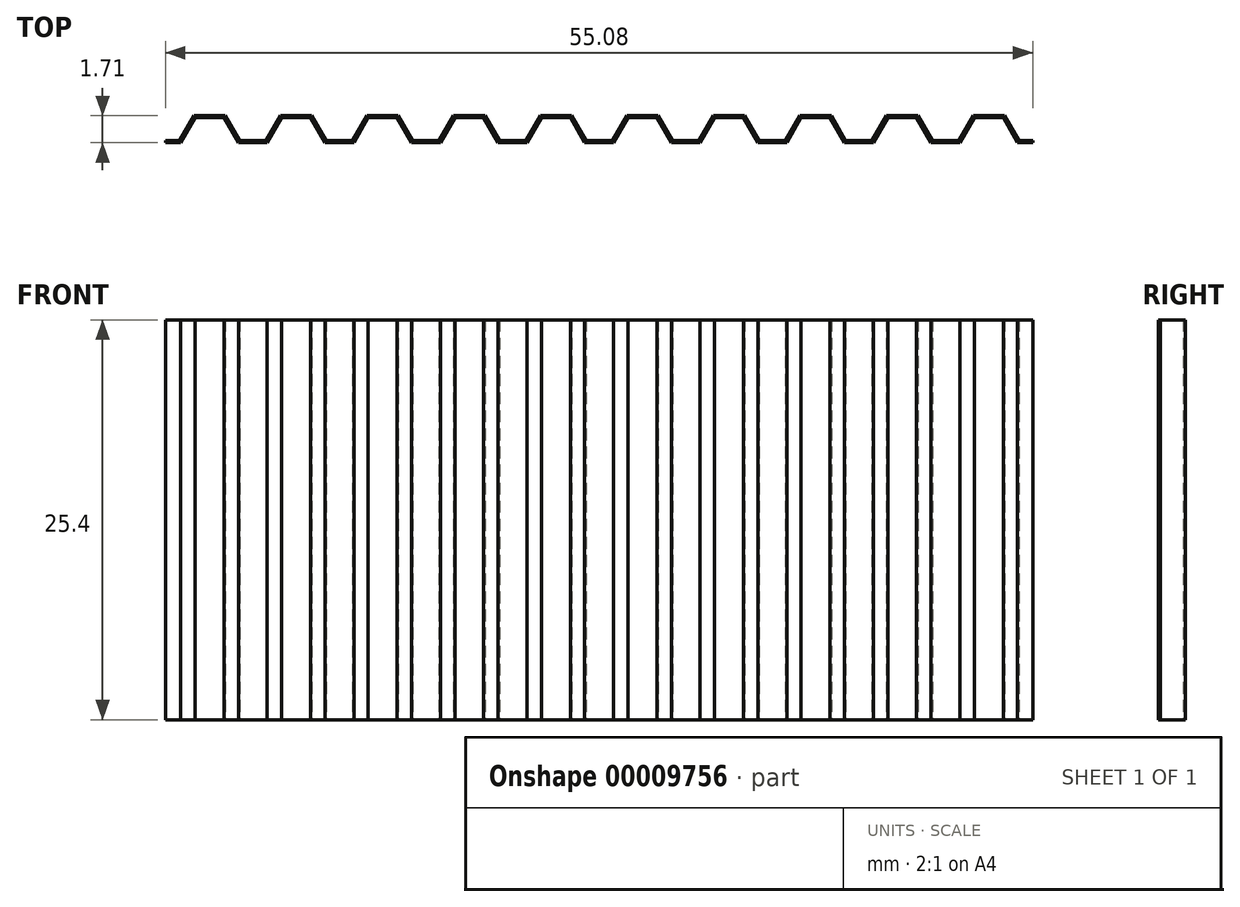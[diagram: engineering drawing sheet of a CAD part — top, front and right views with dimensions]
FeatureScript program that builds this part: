
annotation { "Feature Type Name" : "Feature", "Feature Type Description" : "" }
export const myFeature = defineFeature(function(context is Context, id is Id, definition is map)
    precondition{}
    {
        {
            var Q0;
            Q0=qCreatedBy(makeId("Top.planeOp"),FACE);
            var sketch = newSketch(context, id + "F0", { "sketchPlane" : qUnion([Q0])});
            skCircle(sketch, "E0.cCircle", {"center": v(0, 0) * mm, "radius": 1.59 * mm, "construction": true});
            skLineSegment(sketch, "E0.1", {"start": v(-1.83, 0) * mm, "end": v(-0.92, 1.59) * mm});
            skLineSegment(sketch, "E0.2", {"start": v(-0.92, 1.59) * mm, "end": v(0.92, 1.59) * mm});
            skLineSegment(sketch, "E0.3", {"start": v(0.92, 1.59) * mm, "end": v(1.83, 0) * mm});
            skLineSegment(sketch, "E1", {"start": v(1.83, 0) * mm, "end": v(3.67, 0) * mm});
            skLineSegment(sketch, "E2.1.0.0", {"start": v(6.42, 1.59) * mm, "end": v(7.33, 0) * mm});
            skLineSegment(sketch, "E2.1.0.1", {"start": v(7.33, 0) * mm, "end": v(9.17, 0) * mm});
            skLineSegment(sketch, "E2.1.0.2", {"start": v(3.67, 0) * mm, "end": v(4.58, 1.59) * mm});
            skLineSegment(sketch, "E2.1.0.3", {"start": v(4.58, 1.59) * mm, "end": v(6.42, 1.59) * mm});
            skLineSegment(sketch, "E2.direction1", {"start": v(1.83, 0) * mm, "end": v(7.33, 0) * mm, "construction": true});
            skLineSegment(sketch, "E3.1", {"start": v(7.4, 0.13) * mm, "end": v(9.1, 0.13) * mm});
            skLineSegment(sketch, "E3.2", {"start": v(6.49, 1.71) * mm, "end": v(7.4, 0.13) * mm});
            skLineSegment(sketch, "E3.3", {"start": v(4.5, 1.71) * mm, "end": v(6.49, 1.71) * mm});
            skLineSegment(sketch, "E3.4", {"start": v(3.6, 0.13) * mm, "end": v(4.5, 1.71) * mm});
            skLineSegment(sketch, "E3.5", {"start": v(1.9, 0.13) * mm, "end": v(3.6, 0.13) * mm});
            skLineSegment(sketch, "E3.6", {"start": v(0.99, 1.71) * mm, "end": v(1.9, 0.13) * mm});
            skLineSegment(sketch, "E3.7", {"start": v(-0.99, 1.71) * mm, "end": v(0.99, 1.71) * mm});
            skLineSegment(sketch, "E3.8", {"start": v(-1.9, 0.13) * mm, "end": v(-0.99, 1.71) * mm});
            skLineSegment(sketch, "E4", {"start": v(-1.83, 0) * mm, "end": v(-2.8, 0) * mm});
            skLineSegment(sketch, "E5.0.2.0", {"start": v(11.92, 1.59) * mm, "end": v(12.83, 0) * mm});
            skLineSegment(sketch, "E5.3.2.0", {"start": v(12.83, 0) * mm, "end": v(14.66, 0) * mm});
            skLineSegment(sketch, "E5.6.2.0", {"start": v(9.17, 0) * mm, "end": v(10.08, 1.59) * mm});
            skLineSegment(sketch, "E5.9.2.0", {"start": v(10.08, 1.59) * mm, "end": v(11.92, 1.59) * mm});
            skLineSegment(sketch, "E5.0.3.0", {"start": v(17.41, 1.59) * mm, "end": v(18.33, 0) * mm});
            skLineSegment(sketch, "E5.3.3.0", {"start": v(18.33, 0) * mm, "end": v(20.16, 0) * mm});
            skLineSegment(sketch, "E5.6.3.0", {"start": v(14.66, 0) * mm, "end": v(15.58, 1.59) * mm});
            skLineSegment(sketch, "E5.9.3.0", {"start": v(15.58, 1.59) * mm, "end": v(17.41, 1.59) * mm});
            skLineSegment(sketch, "E5.0.4.0", {"start": v(22.91, 1.59) * mm, "end": v(23.83, 0) * mm});
            skLineSegment(sketch, "E5.3.4.0", {"start": v(23.83, 0) * mm, "end": v(25.66, 0) * mm});
            skLineSegment(sketch, "E5.6.4.0", {"start": v(20.16, 0) * mm, "end": v(21.08, 1.59) * mm});
            skLineSegment(sketch, "E5.9.4.0", {"start": v(21.08, 1.59) * mm, "end": v(22.91, 1.59) * mm});
            skLineSegment(sketch, "E6.0", {"start": v(23.9, 0.13) * mm, "end": v(25.59, 0.13) * mm});
            skLineSegment(sketch, "E6.1", {"start": v(22.99, 1.71) * mm, "end": v(23.9, 0.13) * mm});
            skLineSegment(sketch, "E6.2", {"start": v(21, 1.71) * mm, "end": v(22.99, 1.71) * mm});
            skLineSegment(sketch, "E6.3", {"start": v(20.1, 0.13) * mm, "end": v(21, 1.71) * mm});
            skLineSegment(sketch, "E6.4", {"start": v(18.4, 0.13) * mm, "end": v(20.1, 0.13) * mm});
            skLineSegment(sketch, "E6.5", {"start": v(17.49, 1.71) * mm, "end": v(18.4, 0.13) * mm});
            skLineSegment(sketch, "E6.6", {"start": v(15.5, 1.71) * mm, "end": v(17.49, 1.71) * mm});
            skLineSegment(sketch, "E6.7", {"start": v(14.6, 0.13) * mm, "end": v(15.5, 1.71) * mm});
            skLineSegment(sketch, "E6.8", {"start": v(12.9, 0.13) * mm, "end": v(14.6, 0.13) * mm});
            skLineSegment(sketch, "E6.9", {"start": v(11.99, 1.71) * mm, "end": v(12.9, 0.13) * mm});
            skLineSegment(sketch, "E6.10", {"start": v(10, 1.71) * mm, "end": v(11.99, 1.71) * mm});
            skLineSegment(sketch, "E6.11", {"start": v(9.1, 0.13) * mm, "end": v(10, 1.71) * mm});
            skLineSegment(sketch, "E7.0.5.0", {"start": v(28.41, 1.59) * mm, "end": v(29.33, 0) * mm});
            skLineSegment(sketch, "E7.3.5.0", {"start": v(29.33, 0) * mm, "end": v(31.16, 0) * mm});
            skLineSegment(sketch, "E7.6.5.0", {"start": v(25.66, 0) * mm, "end": v(26.58, 1.59) * mm});
            skLineSegment(sketch, "E7.9.5.0", {"start": v(26.58, 1.59) * mm, "end": v(28.41, 1.59) * mm});
            skLineSegment(sketch, "E7.0.6.0", {"start": v(33.91, 1.59) * mm, "end": v(34.83, 0) * mm});
            skLineSegment(sketch, "E7.3.6.0", {"start": v(34.83, 0) * mm, "end": v(36.66, 0) * mm});
            skLineSegment(sketch, "E7.6.6.0", {"start": v(31.16, 0) * mm, "end": v(32.08, 1.59) * mm});
            skLineSegment(sketch, "E7.9.6.0", {"start": v(32.08, 1.59) * mm, "end": v(33.91, 1.59) * mm});
            skLineSegment(sketch, "E7.0.7.0", {"start": v(39.41, 1.59) * mm, "end": v(40.33, 0) * mm});
            skLineSegment(sketch, "E7.3.7.0", {"start": v(40.33, 0) * mm, "end": v(42.16, 0) * mm});
            skLineSegment(sketch, "E7.6.7.0", {"start": v(36.66, 0) * mm, "end": v(37.58, 1.59) * mm});
            skLineSegment(sketch, "E7.9.7.0", {"start": v(37.58, 1.59) * mm, "end": v(39.41, 1.59) * mm});
            skLineSegment(sketch, "E7.0.8.0", {"start": v(44.91, 1.59) * mm, "end": v(45.83, 0) * mm});
            skLineSegment(sketch, "E7.3.8.0", {"start": v(45.83, 0) * mm, "end": v(47.66, 0) * mm});
            skLineSegment(sketch, "E7.6.8.0", {"start": v(42.16, 0) * mm, "end": v(43.08, 1.59) * mm});
            skLineSegment(sketch, "E7.9.8.0", {"start": v(43.08, 1.59) * mm, "end": v(44.91, 1.59) * mm});
            skLineSegment(sketch, "E7.0.9.0", {"start": v(50.41, 1.59) * mm, "end": v(51.33, 0) * mm});
            skLineSegment(sketch, "E7.6.9.0", {"start": v(47.66, 0) * mm, "end": v(48.58, 1.59) * mm});
            skLineSegment(sketch, "E7.9.9.0", {"start": v(48.58, 1.59) * mm, "end": v(50.41, 1.59) * mm});
            skLineSegment(sketch, "E8.0", {"start": v(51.4, 0.13) * mm, "end": v(52.28, 0.13) * mm});
            skLineSegment(sketch, "E8.1", {"start": v(50.48, 1.71) * mm, "end": v(51.4, 0.13) * mm});
            skLineSegment(sketch, "E8.2", {"start": v(48.5, 1.71) * mm, "end": v(50.48, 1.71) * mm});
            skLineSegment(sketch, "E8.3", {"start": v(47.59, 0.13) * mm, "end": v(48.5, 1.71) * mm});
            skLineSegment(sketch, "E8.4", {"start": v(45.9, 0.13) * mm, "end": v(47.59, 0.13) * mm});
            skLineSegment(sketch, "E8.5", {"start": v(44.98, 1.71) * mm, "end": v(45.9, 0.13) * mm});
            skLineSegment(sketch, "E8.6", {"start": v(43, 1.71) * mm, "end": v(44.98, 1.71) * mm});
            skLineSegment(sketch, "E8.7", {"start": v(42.09, 0.13) * mm, "end": v(43, 1.71) * mm});
            skLineSegment(sketch, "E8.8", {"start": v(40.4, 0.13) * mm, "end": v(42.09, 0.13) * mm});
            skLineSegment(sketch, "E8.9", {"start": v(39.48, 1.71) * mm, "end": v(40.4, 0.13) * mm});
            skLineSegment(sketch, "E8.10", {"start": v(37.5, 1.71) * mm, "end": v(39.48, 1.71) * mm});
            skLineSegment(sketch, "E8.11", {"start": v(36.59, 0.13) * mm, "end": v(37.5, 1.71) * mm});
            skLineSegment(sketch, "E8.12", {"start": v(34.9, 0.13) * mm, "end": v(36.59, 0.13) * mm});
            skLineSegment(sketch, "E8.13", {"start": v(33.99, 1.71) * mm, "end": v(34.9, 0.13) * mm});
            skLineSegment(sketch, "E8.14", {"start": v(32, 1.71) * mm, "end": v(33.99, 1.71) * mm});
            skLineSegment(sketch, "E8.15", {"start": v(31.09, 0.13) * mm, "end": v(32, 1.71) * mm});
            skLineSegment(sketch, "E8.16", {"start": v(29.4, 0.13) * mm, "end": v(31.09, 0.13) * mm});
            skLineSegment(sketch, "E8.17", {"start": v(28.49, 1.71) * mm, "end": v(29.4, 0.13) * mm});
            skLineSegment(sketch, "E8.18", {"start": v(26.5, 1.71) * mm, "end": v(28.49, 1.71) * mm});
            skLineSegment(sketch, "E9.0", {"start": v(25.59, 0.13) * mm, "end": v(26.5, 1.71) * mm});
            skLineSegment(sketch, "E10", {"start": v(52.28, 0.13) * mm, "end": v(52.28, 0) * mm});
            skLineSegment(sketch, "E11", {"start": v(51.33, 0) * mm, "end": v(52.28, 0) * mm});
            skLineSegment(sketch, "E12", {"start": v(1.9, 0.13) * mm, "end": v(1.58, 0.13) * mm});
            skLineSegment(sketch, "E13", {"start": v(-2.8, 0.13) * mm, "end": v(-2.8, 0) * mm});
            skLineSegment(sketch, "E14.trimOffspring", {"start": v(-1.9, 0.13) * mm, "end": v(-2.8, 0.13) * mm});
            skSolve(sketch);
        }
        {
            var Q0;
            Q0 = qSketchRegion(id + "F0", true);
            extrude(context, id + "F1", {"entities" : qUnion([Q0]), "depth" : 25.4 * mm});
        }
    });
